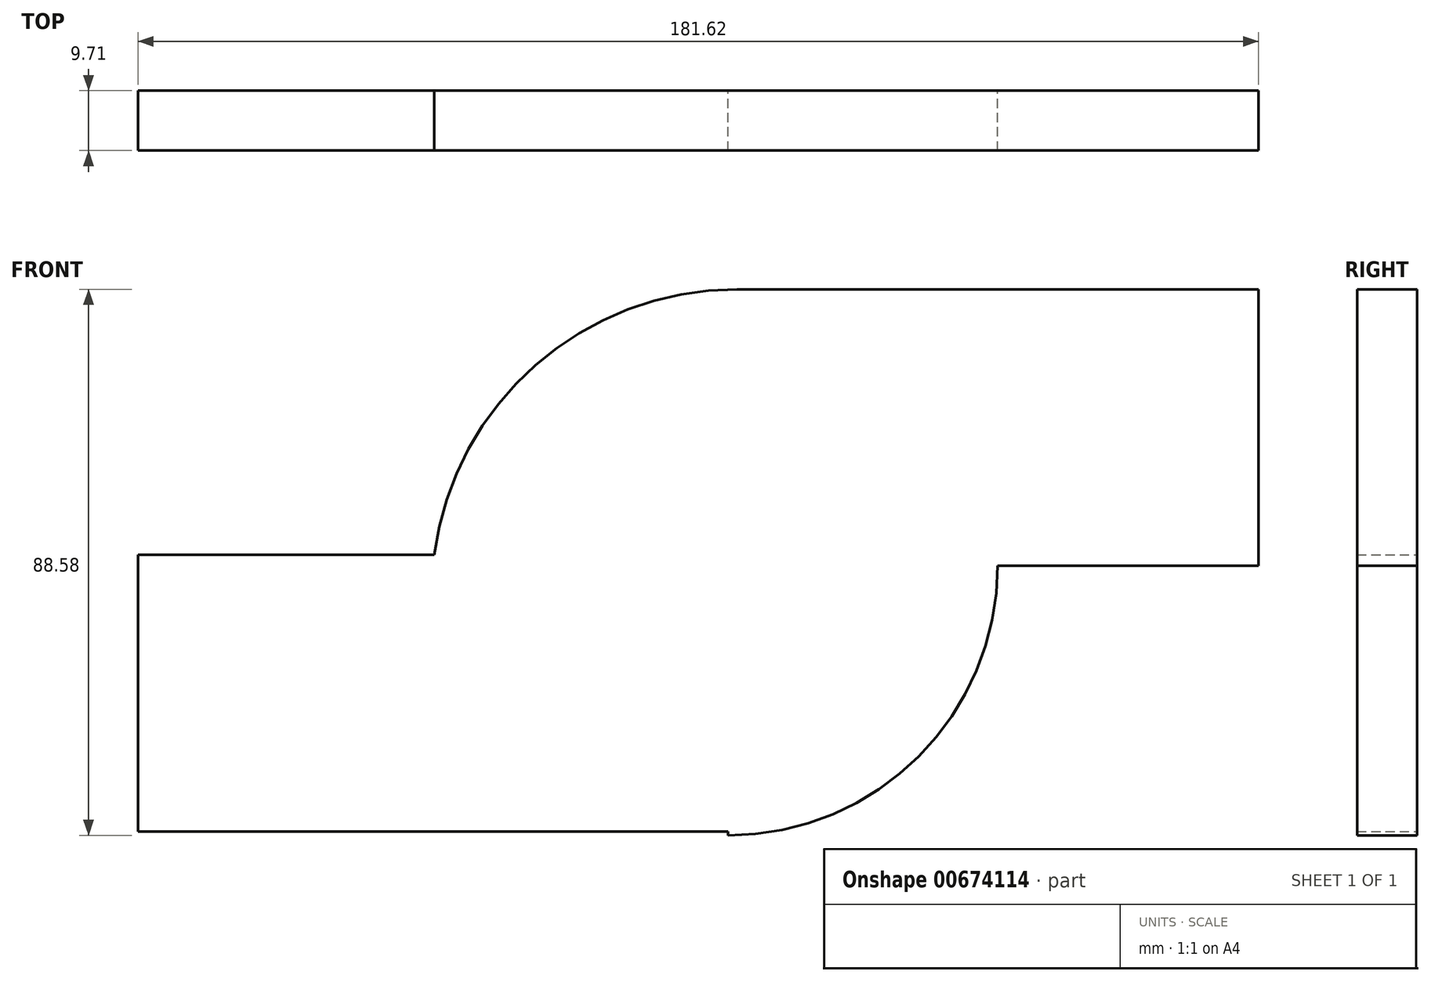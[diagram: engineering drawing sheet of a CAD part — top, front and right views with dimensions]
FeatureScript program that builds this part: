
annotation { "Feature Type Name" : "Feature", "Feature Type Description" : "" }
export const myFeature = defineFeature(function(context is Context, id is Id, definition is map)
    precondition{}
    {
        {
            var Q0;
            Q0=qCreatedBy(makeId("Front.planeOp"),FACE);
            var sketch = newSketch(context, id + "F0", { "sketchPlane" : qUnion([Q0])});
            skLineSegment(sketch, "E0.bottom", {"start": v(-95.62, -43.12) * mm, "end": v(0.39, -43.12) * mm});
            skLineSegment(sketch, "E0.top", {"start": v(-95.62, 1.8) * mm, "end": v(-47.61, 1.8) * mm});
            skLineSegment(sketch, "E0.left", {"start": v(-95.62, -43.12) * mm, "end": v(-95.62, 1.8) * mm});
            skPoint(sketch, "E0.middle", {"position": v(-47.61, -20.66) * mm});
            skLineSegment(sketch, "E1.bottom", {"start": v(86, 44.84) * mm, "end": v(1.49, 44.84) * mm});
            skLineSegment(sketch, "E1.top", {"start": v(86, 0) * mm, "end": v(1.49, 0) * mm});
            skLineSegment(sketch, "E1.left", {"start": v(86, 44.84) * mm, "end": v(86, 0) * mm});
            skPoint(sketch, "E1.middle", {"position": v(43.74, 22.42) * mm});
            skArc(sketch, "E2", {"start": v(1.49, 44.84) * mm, "mid": v(-31.16, 32.55) * mm, "end": v(-47.61, 1.8) * mm});
            skArc(sketch, "E3", {"start": v(43.74, 0) * mm, "mid": v(30.93, -30.93) * mm, "end": v(0, -43.74) * mm});
            skLineSegment(sketch, "E4", {"start": v(0, -43.74) * mm, "end": v(0, -43.12) * mm});
            skPoint(sketch, "E0.right.end.orphan", {"position": v(0.39, 1.8) * mm});
            skPoint(sketch, "E5", {"position": v(-82.2, -33.43) * mm});
            skSolve(sketch);
        }
        {
            var Q0;
            Q0 = qSketchRegion(id + "F0", true);
            extrude(context, id + "F1", {"entities" : qUnion([Q0]), "depth" : 9.7 * mm, "offsetDistance" : 25.4 * mm});
        }
    });
